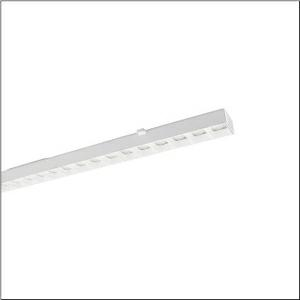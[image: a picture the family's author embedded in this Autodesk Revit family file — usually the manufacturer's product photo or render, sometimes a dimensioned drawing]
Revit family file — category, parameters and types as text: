
# Revit family: silica_r__31_fur_modario_r__31_51ry19mb46c_4938
name_source: partatom
category: Lighting Fixtures
units: mm (PartAtom-declared; Revit-internal decimal feet)

## family parameters
Cut with Voids When Loaded = No
Host = Face
Light Source = No
Part Type = Normal
Room Calculation Point = No
Round Connector Dimension = Use Diameter
Shared = No

## types (1)
- --- (1 x LED, 6620 lm, 37.8 W, 4000K)
    Apparent Load = 38 VA
    CIE Flux Codes = 72 95 99 100 100
    Color Rendering = 80
    Color Temperature = 4000K
    Default Elevation = 1800 mm
    Description = Silica® 31 for Modario® 31, luminaire insert, of aluminium, coated, traffic white (RAL 9016), length: 1.495mm, width: 79mm, height: 62mm, 5x system unit, system units: 299mm, LED rated luminous flux: 6.620lm, light colour: 840, control gear: ON/OFF Multilumen, with system connector: socket, mains connection: 220..240V, AC, 50/60Hz, rated input power: 38W, luminous flux adjustable on luminaire in four steps (3850/4650/5610/6620lm), connected load according to luminous flux setting (21.7/26.2/31.8/37.8W), primary light control with lens, of PMMA, primary anti-glare with reflector, of PC, light emission: direct distribution, primary light characteristic: double asymmetric, protection rating (complete): IP20, insulation class (complete): insulation class I (protective earthing), certification: CE, UKCA, impact resistance: IK02, permissible ambient temperature for indoor applications: -20..+40°C, packaging unit: 1 piece
    Height = 62 mm  [stored 0.203412 ft]
    Lamp = 1 x LED
    Lamp Light Flux = 6620 lm
    Lamp Power = 37.8 W
    Lamp count = 1
    Length = 1495 mm
    Luminous efficacy = 175 lm/W
    Manufacturer = Siteco
    ModVariant = No
    Model = 51RY19MB46C
    Mounting Place = Ceiling
    Mounting Type = Pendant
    Number of Poles = 1
    OnlyDefault = Yes
    Power Factor = 1
    Product Name = Silica® 31 für Modario® 31
    Product group = luminaire insert | ceiling pendant
    ProductGroupID = 902
    Protection Class = Protection class I
    Protection Degree = IP 20
    RLX_Detail_Level = 1
    RLX_Emergency_Light_Flux = 0 lm
    RLX_Emergency_Type = 0
    RLX_Emergency_Type_DB = No
    RlxData = <blob elided: 14069 chars, md5=97943a5d>
    Socket = socket
    Standby Power = 0 W
    System Light Flux = 6620 lm
    System Power = 38 W
    Type Comments = factory setting: luminous flux: 100 % | (OFF | OFF | OFF) | 350 mA
    Type Image = l_1299352.jpg
    URL = http://relux.com
    VarID = @adj_078327
    Voltage = 0 V
    Weight = 0.00 kg
    Width = 79 mm

note: [stored X ft] marks values corroborated as IEEE doubles in the binary element streams (Revit-internal decimal feet)

## geometry (parser evidence)
native form markers: Sweep x11
no freeform markers — native parametric forms only
